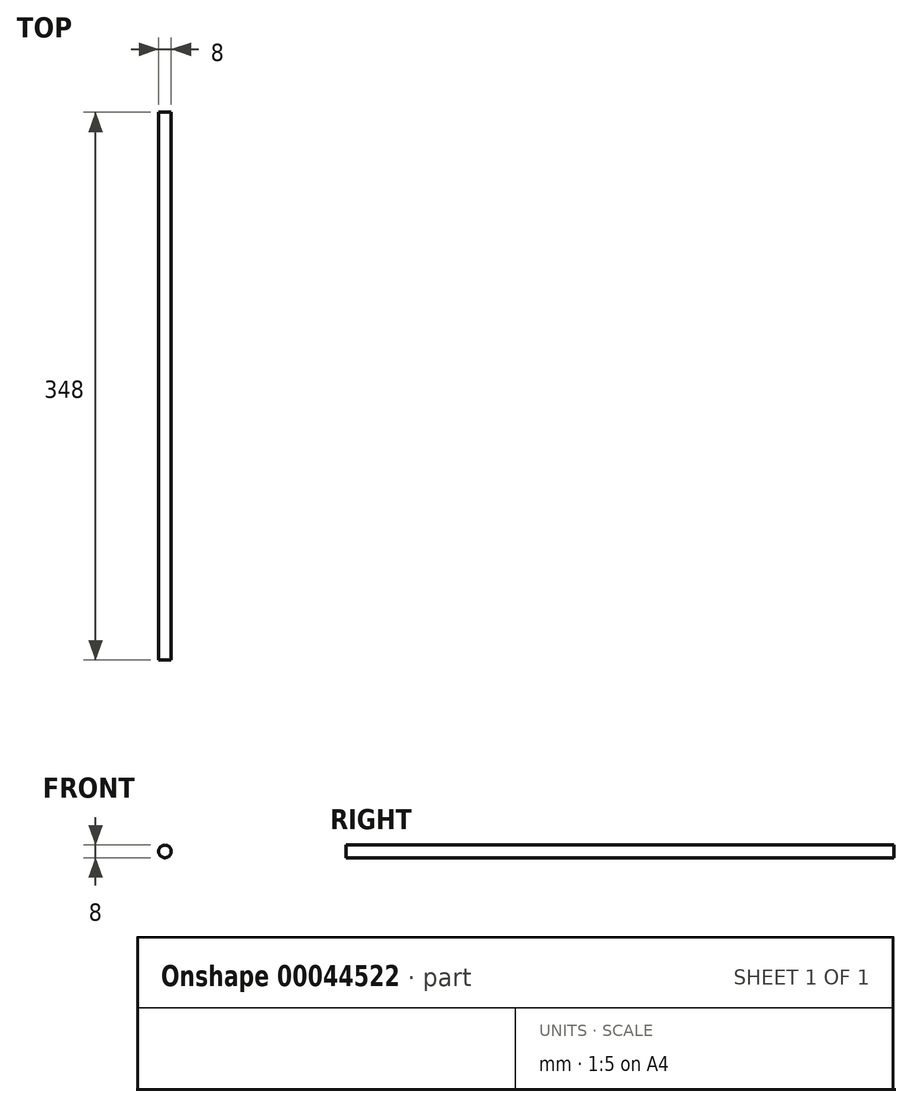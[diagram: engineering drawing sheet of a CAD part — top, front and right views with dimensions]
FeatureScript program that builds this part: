
annotation { "Feature Type Name" : "Feature", "Feature Type Description" : "" }
export const myFeature = defineFeature(function(context is Context, id is Id, definition is map)
    precondition{}
    {
        {
            var Q0;
            Q0=qCreatedBy(makeId("Front.planeOp"),FACE);
            var sketch = newSketch(context, id + "F0", { "sketchPlane" : qUnion([Q0])});
            skCircle(sketch, "E0", {"center": v(0, 0) * mm, "radius": 4 * mm});
            skSolve(sketch);
        }
        {
            var Q0;
            Q0 = qSketchRegion(id + "F0", true);
            extrude(context, id + "F1", {"entities" : qUnion([Q0]), "depth" : 348 * mm});
        }
    });
